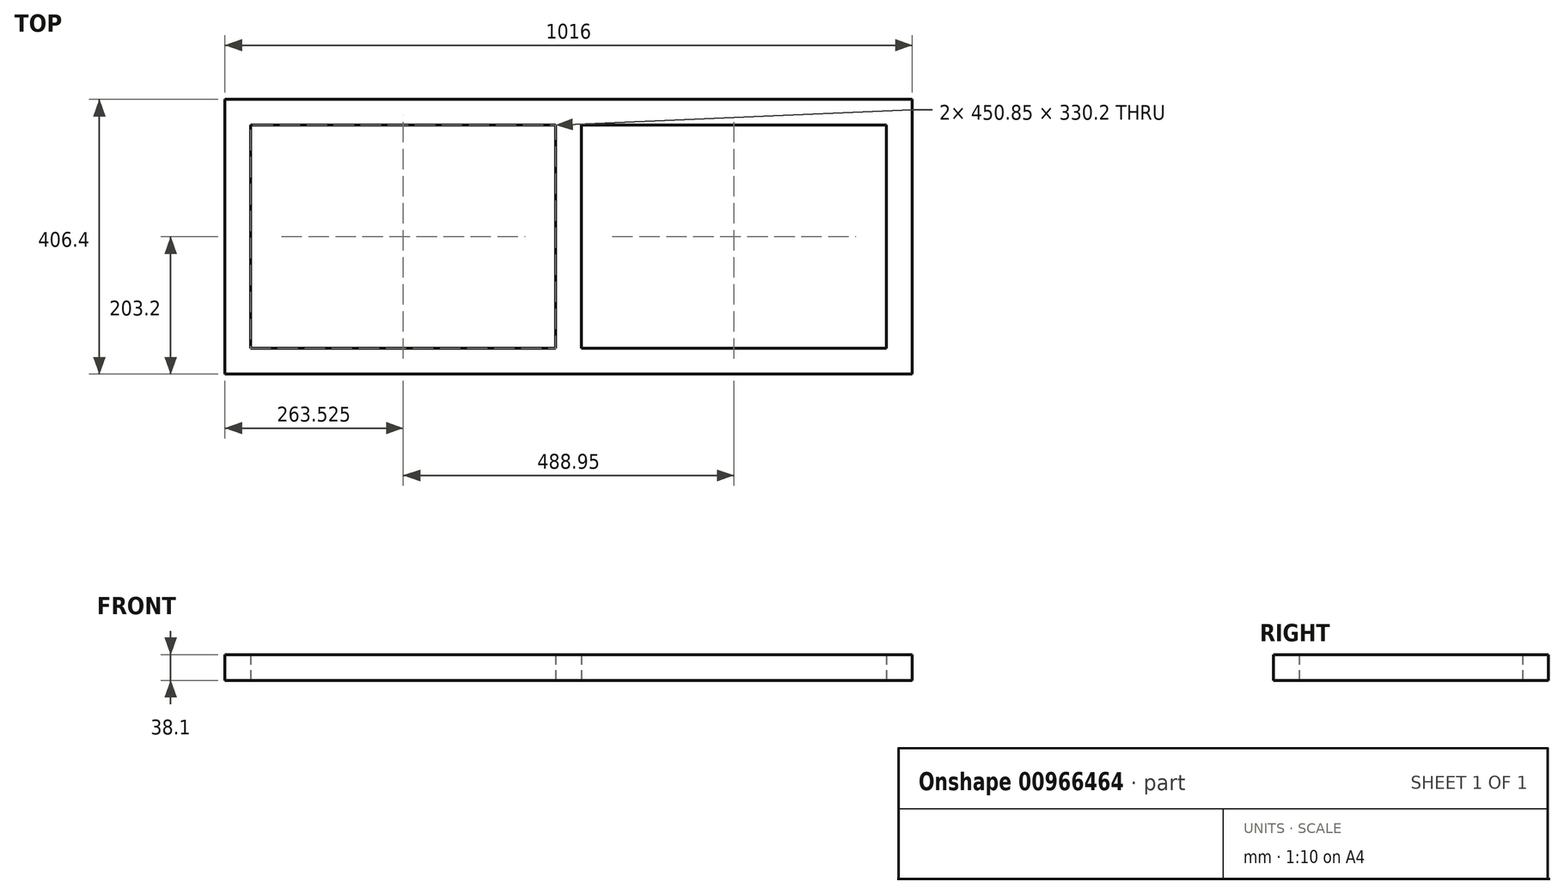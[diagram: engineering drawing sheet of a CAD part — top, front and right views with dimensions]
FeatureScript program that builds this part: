
annotation { "Feature Type Name" : "Feature", "Feature Type Description" : "" }
export const myFeature = defineFeature(function(context is Context, id is Id, definition is map)
    precondition{}
    {
        {
            var Q0;
            Q0=qCreatedBy(makeId("Top.planeOp"),FACE);
            var sketch = newSketch(context, id + "F0", { "sketchPlane" : qUnion([Q0])});
            skLineSegment(sketch, "E0.bottom", {"start": v(508, -203.2) * mm, "end": v(-508, -203.2) * mm});
            skLineSegment(sketch, "E0.top", {"start": v(508, 203.2) * mm, "end": v(-508, 203.2) * mm});
            skLineSegment(sketch, "E0.left", {"start": v(508, -203.2) * mm, "end": v(508, 203.2) * mm});
            skLineSegment(sketch, "E0.right", {"start": v(-508, -203.2) * mm, "end": v(-508, 203.2) * mm});
            skPoint(sketch, "E0.middle", {"position": v(0, 0) * mm});
            skLineSegment(sketch, "E1.bottom", {"start": v(469.9, -165.1) * mm, "end": v(-469.9, -165.1) * mm});
            skLineSegment(sketch, "E1.top", {"start": v(469.9, 165.1) * mm, "end": v(-469.9, 165.1) * mm});
            skLineSegment(sketch, "E1.left", {"start": v(469.9, -165.1) * mm, "end": v(469.9, 165.1) * mm});
            skLineSegment(sketch, "E1.right", {"start": v(-469.9, -165.1) * mm, "end": v(-469.9, 165.1) * mm});
            skLineSegment(sketch, "E2.bottom", {"start": v(19.05, -165.1) * mm, "end": v(-19.05, -165.1) * mm});
            skLineSegment(sketch, "E2.top", {"start": v(19.05, 165.1) * mm, "end": v(-19.05, 165.1) * mm});
            skLineSegment(sketch, "E2.left", {"start": v(19.05, -165.1) * mm, "end": v(19.05, 165.1) * mm});
            skLineSegment(sketch, "E2.right", {"start": v(-19.05, -165.1) * mm, "end": v(-19.05, 165.1) * mm});
            skSolve(sketch);
        }
        {
            var Q0;
            Q0=makeQuery(id+"F0.imprint","IMPRINT",FACE,{"disambiguationData":[TD([[makeQuery(id+"F0.imprint","IMPRINT",EDGE,{"derivedFrom":sQuery(id+"F0.wireOp",EDGE,"E0.bottom")}),-1.0]])]});
            var Q1;
            {var subQ2=sQuery(id+"F0.wireOp",EDGE,"E2.left");Q1=makeQuery(id+"F0.imprint","IMPRINT",FACE,{"disambiguationData":[TD([[makeQuery(id+"F0.imprint","IMPRINT",EDGE,{"derivedFrom":subQ2}),1.0]])]});}
            extrude(context, id + "F1", {"entities" : qUnion([Q0, Q1]), "depth" : 38.1 * mm, "offsetDistance" : 25.4 * mm});
        }
    });
